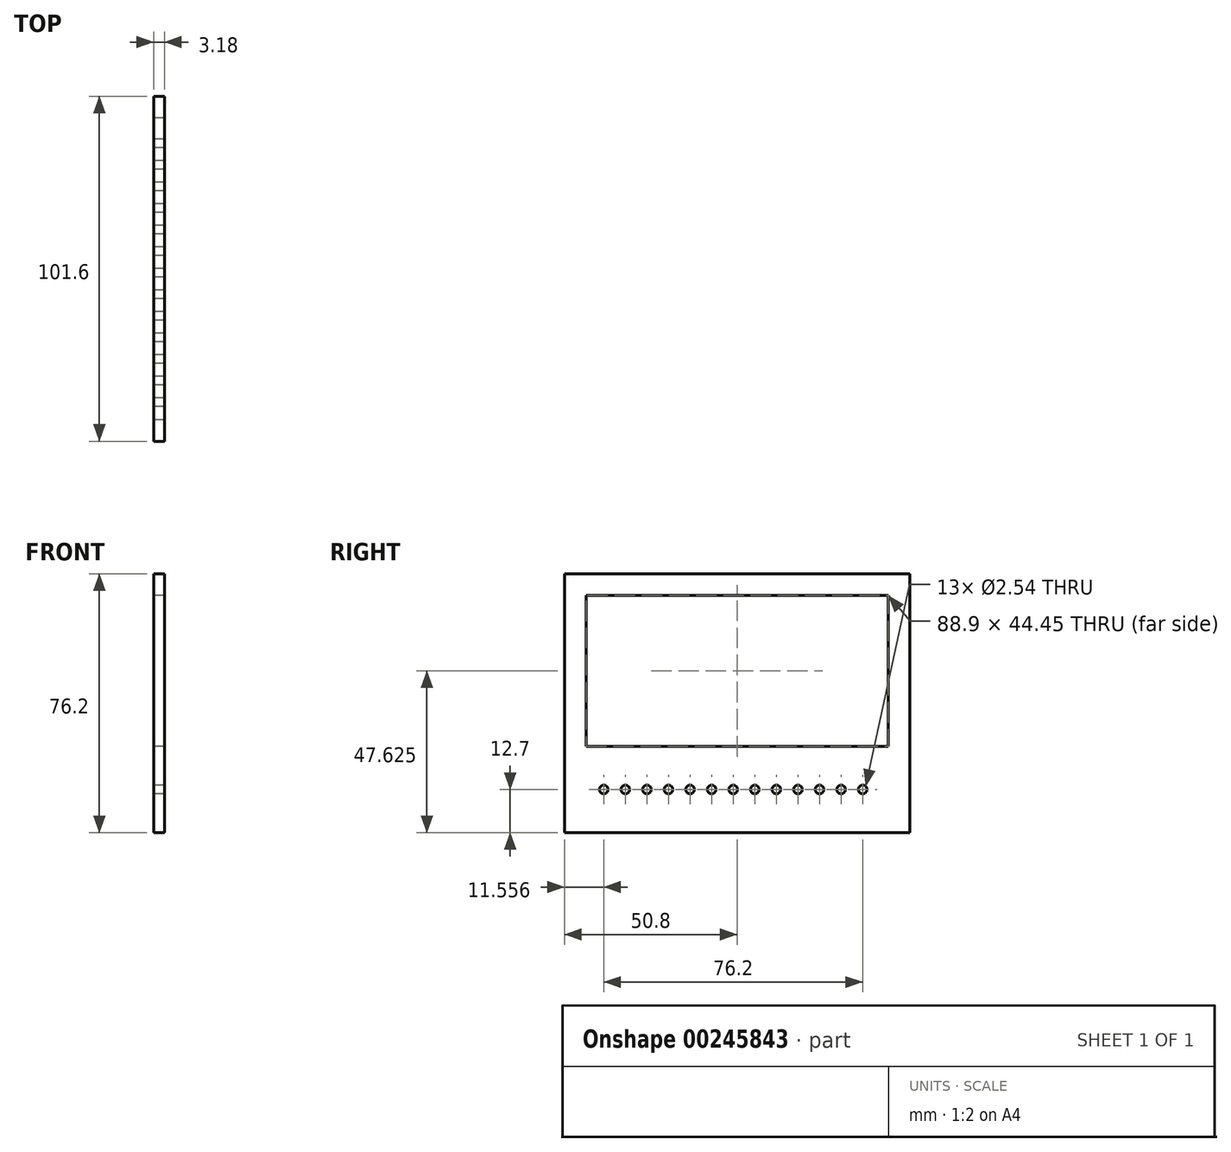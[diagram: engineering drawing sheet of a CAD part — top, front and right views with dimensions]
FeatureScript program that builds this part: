
annotation { "Feature Type Name" : "Feature", "Feature Type Description" : "" }
export const myFeature = defineFeature(function(context is Context, id is Id, definition is map)
    precondition{}
    {
        {
            var Q0;
            Q0=qCreatedBy(makeId("Right.planeOp"),FACE);
            var sketch = newSketch(context, id + "F0", { "sketchPlane" : qUnion([Q0])});
            skLineSegment(sketch, "E0.bottom", {"start": v(50.8, -38.1) * mm, "end": v(-50.8, -38.1) * mm});
            skLineSegment(sketch, "E0.top", {"start": v(50.8, 38.1) * mm, "end": v(-50.8, 38.1) * mm});
            skLineSegment(sketch, "E0.left", {"start": v(50.8, -38.1) * mm, "end": v(50.8, 38.1) * mm});
            skLineSegment(sketch, "E0.right", {"start": v(-50.8, -38.1) * mm, "end": v(-50.8, 38.1) * mm});
            skPoint(sketch, "E0.middle", {"position": v(0, 0) * mm});
            skCircle(sketch, "E1", {"center": v(36.96, -25.4) * mm, "radius": 1.27 * mm});
            skCircle(sketch, "E2.1.0.0", {"center": v(30.6, -25.4) * mm, "radius": 1.27 * mm});
            skCircle(sketch, "E2.2.0.0", {"center": v(24.26, -25.4) * mm, "radius": 1.27 * mm});
            skLineSegment(sketch, "E2.direction1", {"start": v(36.96, -25.4) * mm, "end": v(30.6, -25.4) * mm, "construction": true});
            skCircle(sketch, "E3.0.3.0", {"center": v(17.9, -25.4) * mm, "radius": 1.27 * mm});
            skCircle(sketch, "E3.0.4.0", {"center": v(11.56, -25.4) * mm, "radius": 1.27 * mm});
            skCircle(sketch, "E3.0.5.0", {"center": v(5.2, -25.4) * mm, "radius": 1.27 * mm});
            skCircle(sketch, "E3.0.6.0", {"center": v(-1.14, -25.4) * mm, "radius": 1.27 * mm});
            skCircle(sketch, "E3.0.7.0", {"center": v(-7.5, -25.4) * mm, "radius": 1.27 * mm});
            skCircle(sketch, "E3.0.8.0", {"center": v(-13.84, -25.4) * mm, "radius": 1.27 * mm});
            skCircle(sketch, "E3.0.9.0", {"center": v(-20.2, -25.4) * mm, "radius": 1.27 * mm});
            skCircle(sketch, "E4.0.10.0", {"center": v(-26.54, -25.4) * mm, "radius": 1.27 * mm});
            skCircle(sketch, "E4.0.11.0", {"center": v(-32.9, -25.4) * mm, "radius": 1.27 * mm});
            skCircle(sketch, "E4.0.12.0", {"center": v(-39.24, -25.4) * mm, "radius": 1.27 * mm});
            skLineSegment(sketch, "E5.bottom", {"start": v(44.45, 31.75) * mm, "end": v(-44.45, 31.75) * mm});
            skLineSegment(sketch, "E5.top", {"start": v(44.45, -12.7) * mm, "end": v(-44.45, -12.7) * mm});
            skLineSegment(sketch, "E5.left", {"start": v(44.45, 31.75) * mm, "end": v(44.45, -12.7) * mm});
            skLineSegment(sketch, "E5.right", {"start": v(-44.45, 31.75) * mm, "end": v(-44.45, -12.7) * mm});
            skSolve(sketch);
        }
        {
            var Q0;
            Q0=makeQuery(id+"F0.imprint","IMPRINT",FACE,{"disambiguationData":[TD([[makeQuery(id+"F0.imprint","IMPRINT",EDGE,{"derivedFrom":sQuery(id+"F0.wireOp",EDGE,"E0.bottom")}),-1.0]])]});
            extrude(context, id + "F1", {"entities" : qUnion([Q0]), "depth" : 3.17 * mm});
        }
    });
